# Revit family: Buzzispace - BuzziJet Square1
name_source: partatom
category: Lighting Fixtures
units: mm (PartAtom-declared; Revit-internal decimal feet)

## family parameters
Always vertical = Yes
Cut with Voids When Loaded = No
Host = Ceiling
Light Source = Yes
OmniClass Number = 23.80.70.11
OmniClass Title = Luminaries for Internal Lighting
Part Type = Normal
Room Calculation Point = No
Round Connector Dimension = Use Diameter
Shared = No

## types (6) — shared parameters
Color Filter = 16777215
Dimming Lamp Color Temperature Shift = <None>
Emit Shape Visible in Rendering = No
Light Source Symbol Size = 610 mm
Manufacturer = Buzzispace
URL = https://www.buzzi.space

## per-type parameters (varying)
| type | Cable Count | Cable Offset | Cable Radius | Ceiling Mounted | Corner Radius | Diameter | Emit from Rectangle Length | Emit from Rectangle Width | Height | Light Radius | Model |
| Square S - Ceiling Suspended | 3 | 370 mm  [stored 1.21391 ft] | 200 mm  [stored 0.656168 ft] | No | 190 mm | 800 mm  [stored 2.62467 ft] | 700 mm  [stored 2.29659 ft] | 700 mm  [stored 2.29659 ft] | 225 mm  [stored 0.738189 ft] | 225 mm  [stored 0.738189 ft] | BuzziJet Square S |
| Square M - Ceiling Mounted | 3 | 370 mm  [stored 1.21391 ft] | 200 mm  [stored 0.656168 ft] | Yes | 190 mm | 800 mm  [stored 2.62467 ft] | 700 mm  [stored 2.29659 ft] | 700 mm  [stored 2.29659 ft] | 450 mm  [stored 1.47638 ft] | 225 mm  [stored 0.738189 ft] | BuzziJet Square M |
| Square XXL - Ceiling Suspended | 4 | 705 mm  [stored 2.31299 ft] | 705 mm  [stored 2.31299 ft] | No | 295 mm  [stored 0.967848 ft] | 1470 mm | 1370 mm | 1370 mm | 575 mm | 335 mm  [stored 1.09908 ft] | BuzziJet Square XXL |
| Square XL - Ceiling Suspended | 4 | 570 mm  [stored 1.87008 ft] | 570 mm  [stored 1.87008 ft] | No | 260 mm  [stored 0.853018 ft] | 1200 mm | 1100 mm | 1100 mm | 525 mm | 225 mm  [stored 0.738189 ft] | BuzziJet Square XL |
| Square M - Ceiling Suspended | 3 | 370 mm  [stored 1.21391 ft] | 200 mm  [stored 0.656168 ft] | No | 190 mm | 800 mm  [stored 2.62467 ft] | 700 mm  [stored 2.29659 ft] | 700 mm  [stored 2.29659 ft] | 450 mm  [stored 1.47638 ft] | 225 mm  [stored 0.738189 ft] | BuzziJet Square M |
| Square S - Ceiling Mounted | 3 | 370 mm  [stored 1.21391 ft] | 200 mm  [stored 0.656168 ft] | Yes | 190 mm | 800 mm  [stored 2.62467 ft] | 700 mm  [stored 2.29659 ft] | 700 mm  [stored 2.29659 ft] | 225 mm  [stored 0.738189 ft] | 225 mm  [stored 0.738189 ft] | BuzziJet Square S |

note: [stored X ft] marks values corroborated as IEEE doubles in the binary element streams (Revit-internal decimal feet)

## geometry (parser evidence)
native form markers: Sweep x5
no freeform markers — native parametric forms only
